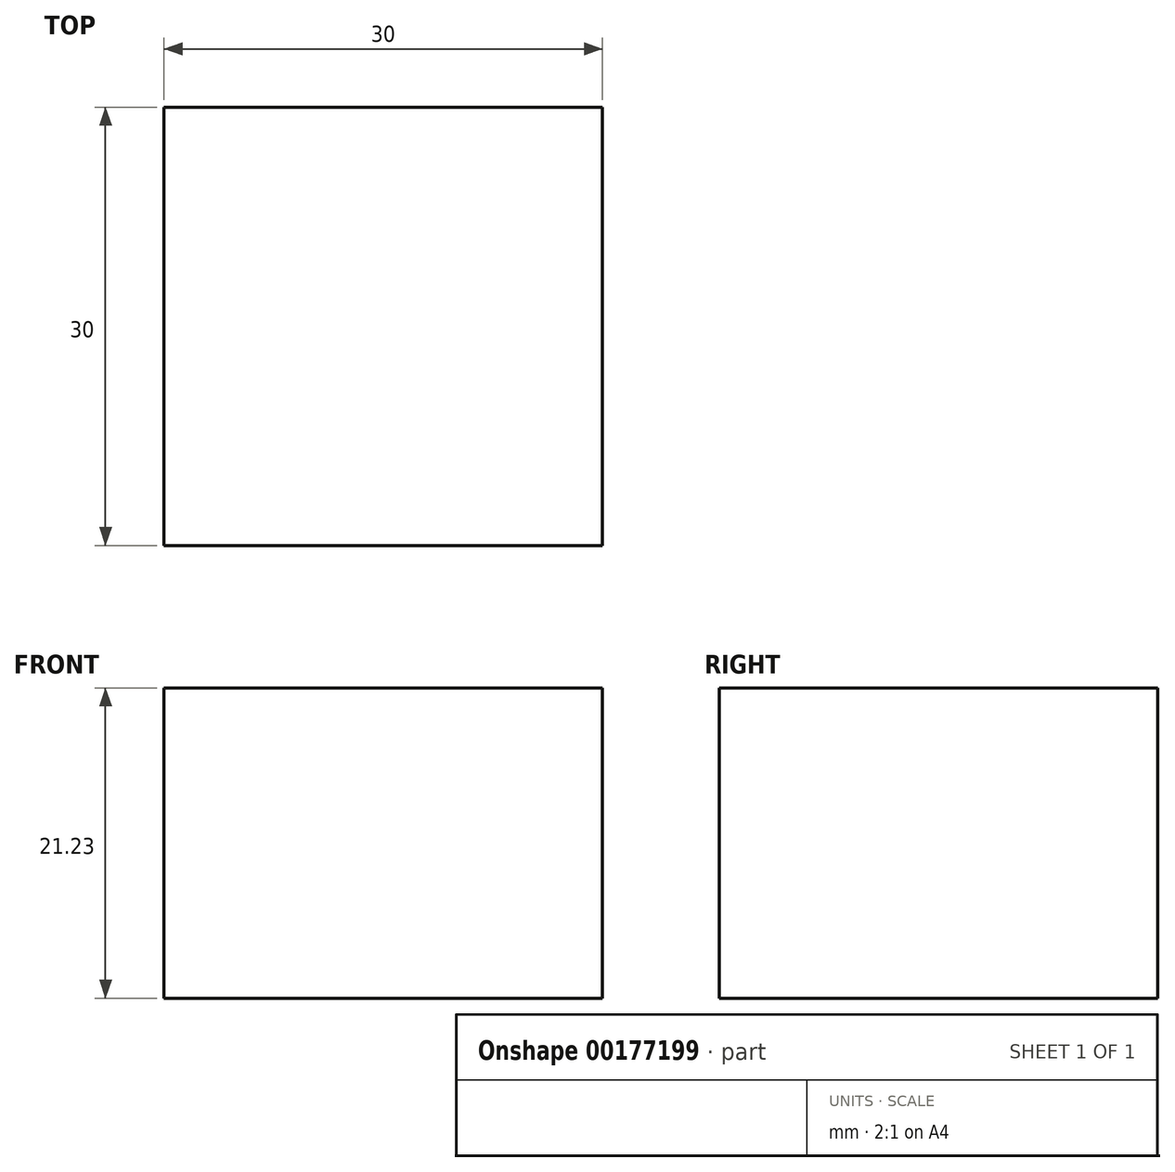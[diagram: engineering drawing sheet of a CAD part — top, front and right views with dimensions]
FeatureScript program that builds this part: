
annotation { "Feature Type Name" : "Feature", "Feature Type Description" : "" }
export const myFeature = defineFeature(function(context is Context, id is Id, definition is map)
    precondition{}
    {
        {
            var Q0;
            Q0=qCreatedBy(makeId("Front.planeOp"),FACE);
            var sketch = newSketch(context, id + "F0", { "sketchPlane" : qUnion([Q0])});
            skLineSegment(sketch, "E0.bottom", {"start": v(15, 15) * mm, "end": v(-15, 15) * mm});
            skLineSegment(sketch, "E0.top", {"start": v(15, -15) * mm, "end": v(-15, -15) * mm});
            skLineSegment(sketch, "E0.left", {"start": v(15, 15) * mm, "end": v(15, -15) * mm});
            skLineSegment(sketch, "E0.right", {"start": v(-15, 15) * mm, "end": v(-15, -15) * mm});
            skPoint(sketch, "E0.middle", {"position": v(0, 0) * mm});
            skSolve(sketch);
        }
        {
            var Q0;
            Q0 = qSketchRegion(id + "F0", true);
            extrude(context, id + "F1", {"entities" : qUnion([Q0]), "endBound" : BoundingType.SYMMETRIC, "depth" : 30 * mm, "offsetDistance" : 25 * mm});
        }
        {
            var Q0;
            Q0=qCreatedBy(makeId("Front.planeOp"),FACE);
            var sketch = newSketch(context, id + "F2", { "sketchPlane" : qUnion([Q0])});
            skLineSegment(sketch, "E1.bottom", {"start": v(-16.96, -16.3) * mm, "end": v(16.29, -16.3) * mm});
            skLineSegment(sketch, "E1.top", {"start": v(-16.96, -6.23) * mm, "end": v(16.29, -6.23) * mm});
            skLineSegment(sketch, "E1.left", {"start": v(-16.96, -16.3) * mm, "end": v(-16.96, -6.23) * mm});
            skLineSegment(sketch, "E1.right", {"start": v(16.29, -16.3) * mm, "end": v(16.29, -6.23) * mm});
            skSolve(sketch);
        }
        {
            var Q0;
            Q0 = qSketchRegion(id + "F2", true);
            extrude(context, id + "F3", {"entities" : qUnion([Q0]), "operationType" : NewBodyOperationType.REMOVE, "endBound" : BoundingType.SYMMETRIC, "oppositeDirection" : true, "depth" : 30 * mm, "offsetDistance" : 25 * mm});
        }
    });
